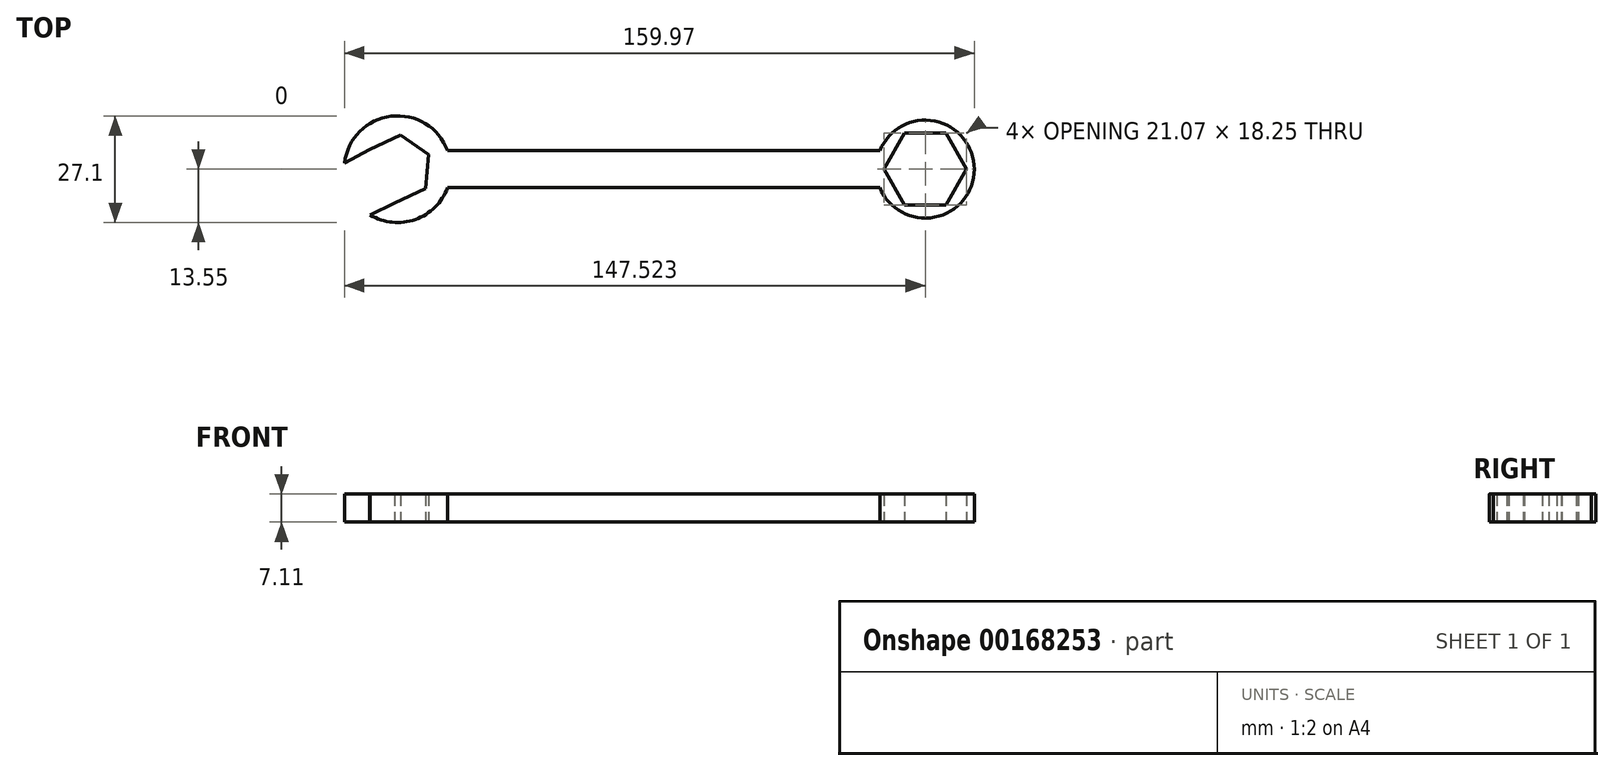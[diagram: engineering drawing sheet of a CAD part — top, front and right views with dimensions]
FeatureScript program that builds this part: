
annotation { "Feature Type Name" : "Feature", "Feature Type Description" : "" }
export const myFeature = defineFeature(function(context is Context, id is Id, definition is map)
    precondition{}
    {
        {
            var Q0;
            Q0=qCreatedBy(makeId("Top.planeOp"),FACE);
            var sketch = newSketch(context, id + "F0", { "sketchPlane" : qUnion([Q0])});
            skArc(sketch, "E0", {"start": v(54.01, -4.7) * mm, "mid": v(77.99, -0.02) * mm, "end": v(54.03, 4.72) * mm});
            skArc(sketch, "E1", {"start": v(-55.82, 4.72) * mm, "mid": v(-70.12, 13.46) * mm, "end": v(-81.98, 1.6) * mm});
            skLineSegment(sketch, "E2", {"start": v(-55.8, -4.7) * mm, "end": v(54.01, -4.7) * mm});
            skLineSegment(sketch, "E3", {"start": v(-55.82, 4.72) * mm, "end": v(54.03, 4.72) * mm});
            skCircle(sketch, "E4.cCircle", {"center": v(65.54, 0) * mm, "radius": 9.12 * mm, "construction": true});
            skLineSegment(sketch, "E4.0", {"start": v(60.28, 9.12) * mm, "end": v(70.8, 9.12) * mm});
            skLineSegment(sketch, "E4.1", {"start": v(70.8, 9.12) * mm, "end": v(76.08, 0) * mm});
            skLineSegment(sketch, "E4.2", {"start": v(76.08, 0) * mm, "end": v(70.8, -9.12) * mm});
            skLineSegment(sketch, "E4.3", {"start": v(70.8, -9.12) * mm, "end": v(60.28, -9.12) * mm});
            skLineSegment(sketch, "E4.4", {"start": v(60.28, -9.12) * mm, "end": v(55, 0) * mm});
            skLineSegment(sketch, "E4.5", {"start": v(55, 0) * mm, "end": v(60.28, 9.12) * mm});
            skPoint(sketch, "E4.0.midPoint", {"position": v(65.54, 9.12) * mm});
            skLineSegment(sketch, "E5.0", {"start": v(-75.61, 4.94) * mm, "end": v(-67.79, 8.61) * mm});
            skLineSegment(sketch, "E5.1", {"start": v(-67.79, 8.61) * mm, "end": v(-60.7, 3.67) * mm});
            skLineSegment(sketch, "E5.2", {"start": v(-60.7, 3.67) * mm, "end": v(-61.43, -4.94) * mm});
            skLineSegment(sketch, "E5.3", {"start": v(-61.43, -4.94) * mm, "end": v(-69.26, -8.61) * mm});
            skPoint(sketch, "E5.0.midPoint", {"position": v(-71.7, 6.78) * mm});
            skLineSegment(sketch, "E6", {"start": v(-75.61, 4.94) * mm, "end": v(-81.98, 1.6) * mm});
            skLineSegment(sketch, "E7", {"start": v(-75.45, -11.65) * mm, "end": v(-69.26, -8.61) * mm});
            skArc(sketch, "E8.trimOffspring", {"start": v(-75.45, -11.65) * mm, "mid": v(-64, -12.78) * mm, "end": v(-55.8, -4.7) * mm});
            skPoint(sketch, "E9.orphan", {"position": v(-85.04, 0) * mm});
            skSolve(sketch);
        }
        {
            var Q0;
            Q0 = qSketchRegion(id + "F0", true);
            extrude(context, id + "F1", {"entities" : qUnion([Q0]), "depth" : 7.11 * mm});
        }
    });
